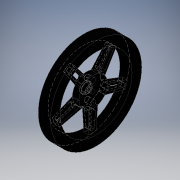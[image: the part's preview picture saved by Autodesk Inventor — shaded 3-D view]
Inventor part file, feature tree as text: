
AUTODESK INVENTOR PART (.ipt)
format: ipt  version: 2016 (Build 200138000, 138)  size: 242,688 bytes
history: native  units: mm
features: sketch x10, extrude x8, pattern_circular x2, plane x2, loft x1
ambient origin geometry x8: Origin, YZ Plane, XZ Plane, XY Plane, X Axis, Y Axis, Z Axis, Center Point
bodies: Solid1 (feature_tree)
feature tree (23):
  extrude  "Extrusion1"  TaperAngle=0.0deg  [1 undecoded]
  extrude  "Extrusion2"  Depth=4.3mm TaperAngle=0.0deg
  extrude  "Extrusion3"  Depth=6.3mm
  extrude  "Extrusion4"  Depth=4.3mm TaperAngle=360.0deg
  pattern_circular  "Circular Pattern1"  [2 undecoded]
  extrude  "Extrusion5"  Depth=2.5mm
  extrude  "Extrusion6"  Depth=2.5mm
  plane  "Work Plane2"
  sketch  "Sketch9"  dims[d21=2.5mm d22=0.0mm]
  plane  "Work Plane3"
  loft  "Loft1"
  extrude  "Extrusion7"  TaperAngle=0.0deg  [1 undecoded]
  extrude  "Extrusion8"  TaperAngle=0.0deg  [1 undecoded]
  pattern_circular  "Circular Pattern3"  [2 undecoded]
  sketch  "Sketch1"  dims[d2=0.0mm d6=0.0mm]
  sketch  "Sketch2"  dims[d7=2.44mm d8=4.3mm d9=0.0mm]
  sketch  "Sketch3"  dims[d10=3.2mm d11=6.3mm]
  sketch  "Sketch4"  dims[d12=4.3mm d13=0.0mm d14=20.0mm d15=360.0deg]
  sketch  "Sketch5"  dims[d18=7.0mm]
  sketch  "Sketch7"  dims[d19=1.14mm d20=0.0mm]
  sketch  "Sketch10"  dims[d23=4.6mm]
  sketch  "Sketch11"  dims[d24=2.15mm]
  sketch  "Sketch12"  dims[d25=4.3mm d26=5.8mm d27=2.9mm d28=3.0mm d29=5.0mm d30=0.0mm d31=90.0deg d32=0.0mm d33=90.0deg d34=2.5mm d35=0.0mm d40=11.9mm d41=21.2mm d42=3.018706mm d43=2.5mm d44=0.0mm d45=50.0mm d46=360.0deg]
note: 7 required parameter values undecoded (feature->parameter linkage not recoverable at this tier; creation-order binding heuristic only, values carry confidence <= 0.55)
